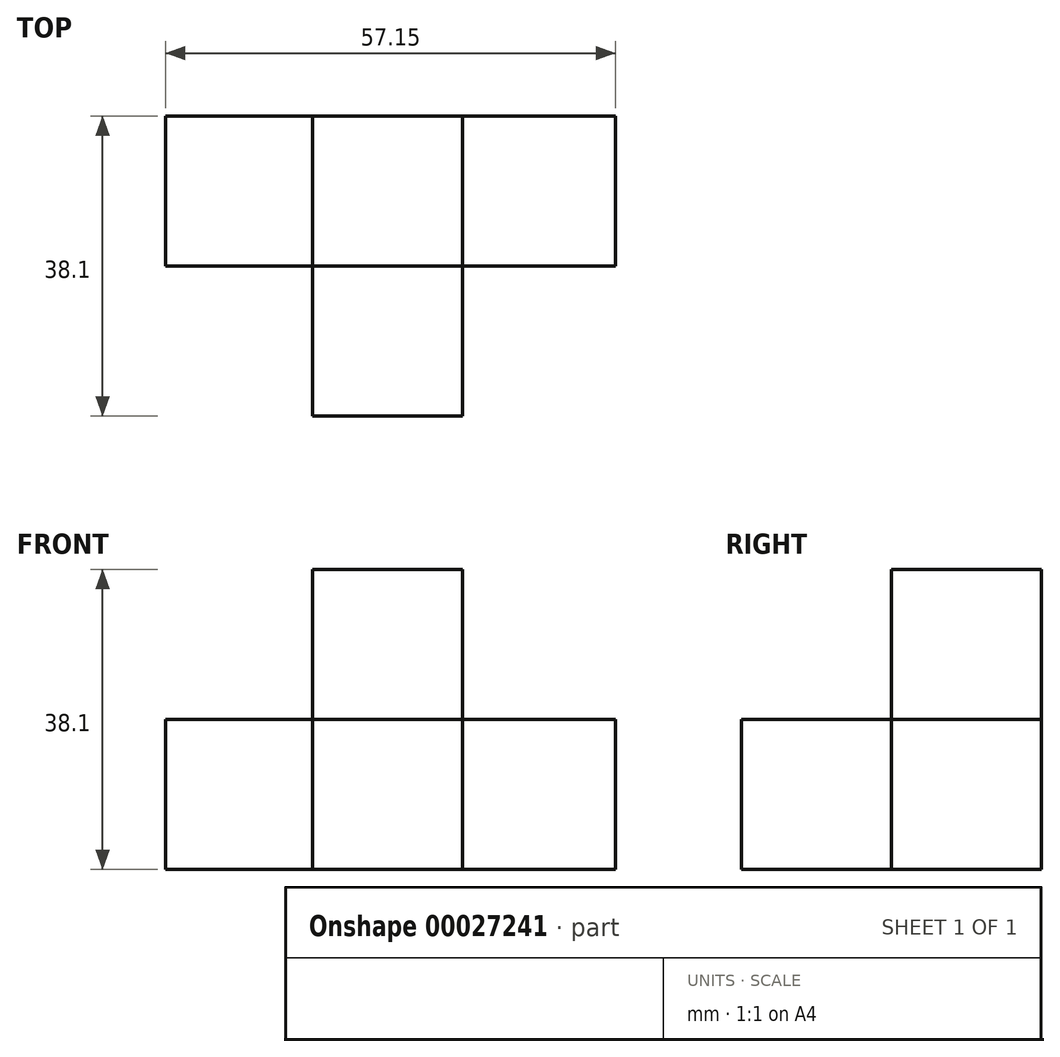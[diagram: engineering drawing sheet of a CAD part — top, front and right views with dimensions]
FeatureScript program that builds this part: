
annotation { "Feature Type Name" : "Feature", "Feature Type Description" : "" }
export const myFeature = defineFeature(function(context is Context, id is Id, definition is map)
    precondition{}
    {
        {
            var Q0;
            Q0=qCreatedBy(makeId("Top.planeOp"),FACE);
            var sketch = newSketch(context, id + "F0", { "sketchPlane" : qUnion([Q0])});
            skLineSegment(sketch, "E0.bottom", {"start": v(-57.15, 0) * mm, "end": v(0, 0) * mm});
            skLineSegment(sketch, "E0.top", {"start": v(-57.15, -19.05) * mm, "end": v(0, -19.05) * mm});
            skLineSegment(sketch, "E0.left", {"start": v(-57.15, 0) * mm, "end": v(-57.15, -19.05) * mm});
            skLineSegment(sketch, "E0.right", {"start": v(0, 0) * mm, "end": v(0, -19.05) * mm});
            skSolve(sketch);
        }
        {
            var Q0;
            Q0=makeQuery(id+"F0.imprint","IMPRINT",FACE,{"disambiguationData":[TD([[makeQuery(id+"F0.imprint","IMPRINT",EDGE,{"derivedFrom":sQuery(id+"F0.wireOp",EDGE,"E0.bottom")}),-1.0]])]});
            extrude(context, id + "F1", {"entities" : qUnion([Q0]), "depth" : 19.05 * mm});
        }
        {
            var Q0;
            Q0=makeQuery(id+"F1.opExtrude","CAP_FACE",FACE,{"disambiguationData":[OSD([sQuery(id+"F0.wireOp",EDGE,"E0.bottom"),sQuery(id+"F0.wireOp",EDGE,"E0.top"),sQuery(id+"F0.wireOp",EDGE,"E0.left"),sQuery(id+"F0.wireOp",EDGE,"E0.right")])],"isStart":false});
            var sketch = newSketch(context, id + "F2", { "sketchPlane" : qUnion([Q0])});
            skLineSegment(sketch, "E1.bottom", {"start": v(-38.5, 0) * mm, "end": v(-19.46, 0) * mm});
            skLineSegment(sketch, "E1.top", {"start": v(-38.5, -19.05) * mm, "end": v(-19.46, -19.05) * mm});
            skLineSegment(sketch, "E1.left", {"start": v(-38.5, 0) * mm, "end": v(-38.5, -19.05) * mm});
            skLineSegment(sketch, "E1.right", {"start": v(-19.46, 0) * mm, "end": v(-19.46, -19.05) * mm});
            skSolve(sketch);
        }
        {
            var Q0;
            Q0=makeQuery(id+"F2.imprint","IMPRINT",FACE,{"disambiguationData":[TD([[makeQuery(id+"F2.imprint","IMPRINT",EDGE,{"derivedFrom":sQuery(id+"F2.wireOp",EDGE,"E1.bottom")}),-1.0]])]});
            extrude(context, id + "F3", {"entities" : qUnion([Q0]), "operationType" : NewBodyOperationType.ADD, "depth" : 19.05 * mm});
        }
        {
            var Q0;
            Q0=makeQuery(id+"F3.boolean.opBoolean","MERGE",FACE,{"derivedFrom":[makeQuery(id+"F1.opExtrude","SWEPT_FACE",FACE,{"disambiguationData":[OSD([sQuery(id+"F0.wireOp",EDGE,"E0.top")])]}),makeQuery(id+"F3.opExtrude","SWEPT_FACE",FACE,{"disambiguationData":[OSD([sQuery(id+"F2.wireOp",EDGE,"E1.top")])]})]});
            var sketch = newSketch(context, id + "F4", { "sketchPlane" : qUnion([Q0])});
            skLineSegment(sketch, "E2.bottom", {"start": v(-38.5, 19.05) * mm, "end": v(-19.46, 19.05) * mm});
            skLineSegment(sketch, "E2.top", {"start": v(-38.5, 0) * mm, "end": v(-19.46, 0) * mm});
            skLineSegment(sketch, "E2.left", {"start": v(-38.5, 19.05) * mm, "end": v(-38.5, 0) * mm});
            skLineSegment(sketch, "E2.right", {"start": v(-19.46, 19.05) * mm, "end": v(-19.46, 0) * mm});
            skSolve(sketch);
        }
        {
            var Q0;
            Q0=makeQuery(id+"F4.imprint","IMPRINT",FACE,{"disambiguationData":[TD([[makeQuery(id+"F4.imprint","IMPRINT",EDGE,{"derivedFrom":sQuery(id+"F4.wireOp",EDGE,"E2.bottom")}),-1.0]])]});
            extrude(context, id + "F5", {"entities" : qUnion([Q0]), "operationType" : NewBodyOperationType.ADD, "depth" : 19.05 * mm});
        }
    });
